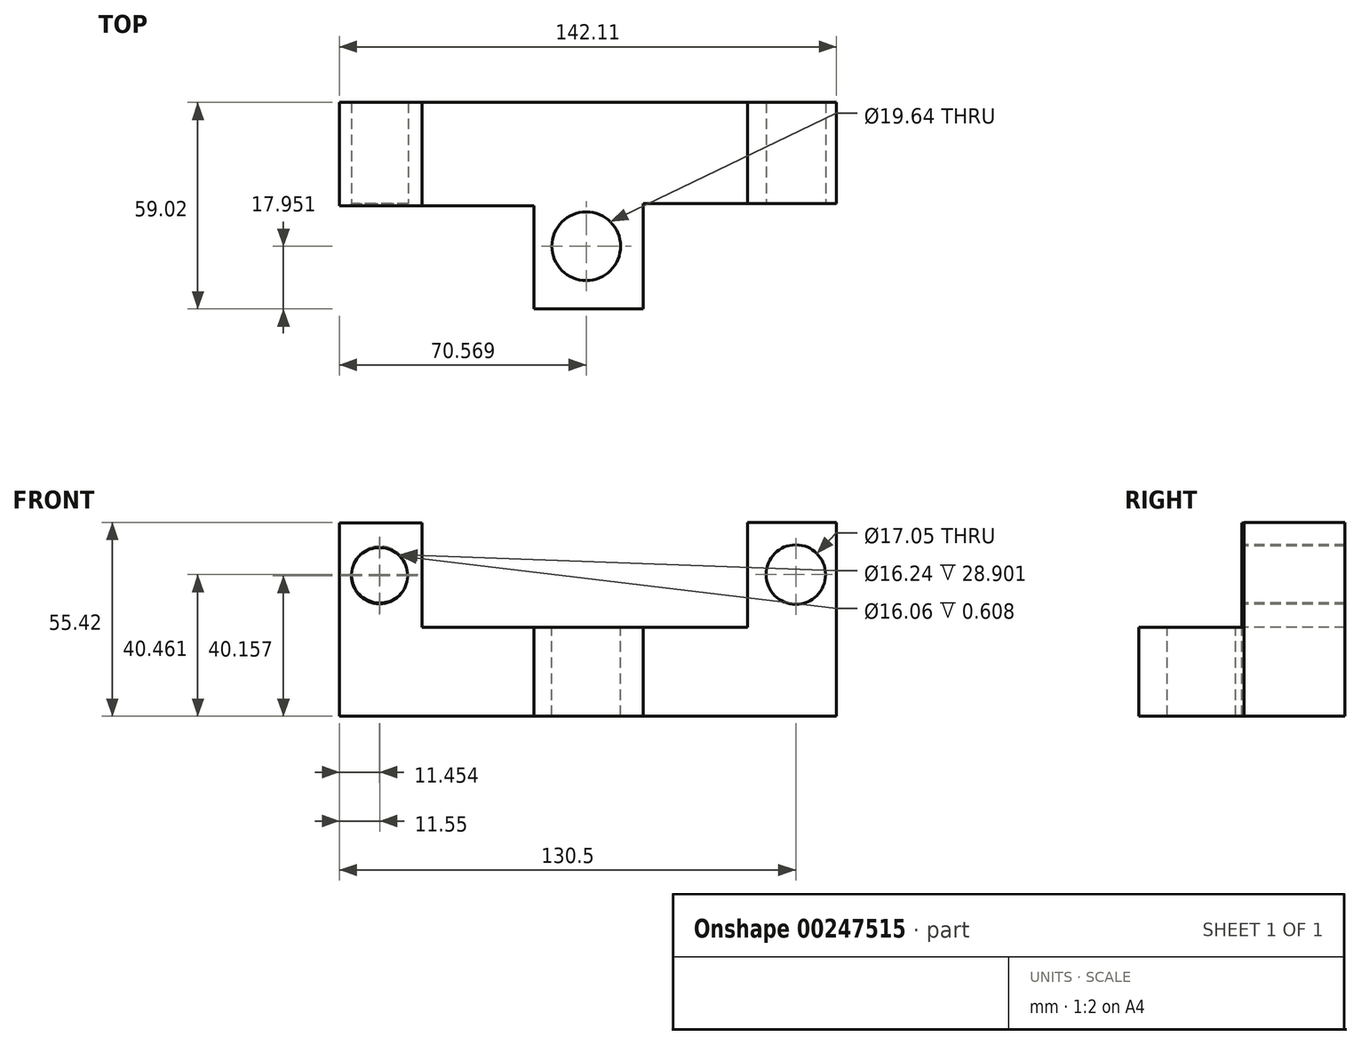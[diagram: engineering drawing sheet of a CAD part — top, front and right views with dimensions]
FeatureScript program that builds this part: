
annotation { "Feature Type Name" : "Feature", "Feature Type Description" : "" }
export const myFeature = defineFeature(function(context is Context, id is Id, definition is map)
    precondition{}
    {
        {
            var Q0;
            Q0=qCreatedBy(makeId("Top.planeOp"),FACE);
            var sketch = newSketch(context, id + "F0", { "sketchPlane" : qUnion([Q0])});
            skLineSegment(sketch, "E0.bottom", {"start": v(-43.05, 28.9) * mm, "end": v(50.04, 28.9) * mm});
            skLineSegment(sketch, "E0.top", {"start": v(-43.05, -30.12) * mm, "end": v(50.04, -30.12) * mm});
            skLineSegment(sketch, "E0.left", {"start": v(-43.05, 28.9) * mm, "end": v(-43.05, -30.12) * mm});
            skLineSegment(sketch, "E0.right", {"start": v(50.04, 28.9) * mm, "end": v(50.04, -30.12) * mm});
            skSolve(sketch);
        }
        {
            var Q0;
            Q0 = qSketchRegion(id + "F0", true);
            extrude(context, id + "F1", {"entities" : qUnion([Q0]), "depth" : 25.4 * mm});
        }
        {
            var Q0;
            Q0=makeQuery(id+"F1.opExtrude","CAP_FACE",FACE,{"disambiguationData":[OSD([sQuery(id+"F0.wireOp",EDGE,"E0.bottom"),sQuery(id+"F0.wireOp",EDGE,"E0.top"),sQuery(id+"F0.wireOp",EDGE,"E0.left"),sQuery(id+"F0.wireOp",EDGE,"E0.right")])],"isStart":false});
            var sketch = newSketch(context, id + "F2", { "sketchPlane" : qUnion([Q0])});
            skLineSegment(sketch, "E1", {"start": v(-43.05, -0.6) * mm, "end": v(-11.1, -0.6) * mm});
            skLineSegment(sketch, "E2", {"start": v(-11.1, -0.6) * mm, "end": v(-11.1, -30.12) * mm});
            skLineSegment(sketch, "E3", {"start": v(20.23, 0) * mm, "end": v(20.23, -30.12) * mm});
            skLineSegment(sketch, "E4", {"start": v(20.23, -30.12) * mm, "end": v(-11.1, -30.12) * mm});
            skLineSegment(sketch, "E5", {"start": v(20.23, 0) * mm, "end": v(50.04, 0) * mm});
            skLineSegment(sketch, "E6", {"start": v(50.04, 0) * mm, "end": v(50.04, -30.12) * mm});
            skLineSegment(sketch, "E7", {"start": v(50.04, -30.12) * mm, "end": v(-43.05, -30.12) * mm});
            skLineSegment(sketch, "E8", {"start": v(-43.05, -30.12) * mm, "end": v(-43.05, -0.6) * mm});
            skSolve(sketch);
        }
        {
            var Q0;
            {var subQ0=sQuery(id+"F2.wireOp",EDGE,"E3");Q0=makeQuery(id+"F2.imprint","IMPRINT",FACE,{"disambiguationData":[TD([[makeQuery(id+"F2.imprint","IMPRINT",EDGE,{"derivedFrom":subQ0}),1.0]])]});}
            var Q1;
            Q1=makeQuery(id+"F2.imprint","IMPRINT",FACE,{"disambiguationData":[TD([[makeQuery(id+"F2.imprint","IMPRINT",EDGE,{"derivedFrom":sQuery(id+"F2.wireOp",EDGE,"E1")}),-1.0]])]});
            extrude(context, id + "F3", {"entities" : qUnion([Q0, Q1]), "operationType" : NewBodyOperationType.REMOVE, "oppositeDirection" : true, "depth" : 25.4 * mm});
        }
        {
            var Q0;
            Q0=makeQuery(id+"F1.opExtrude","SWEPT_FACE",FACE,{"disambiguationData":[OSD([sQuery(id+"F0.wireOp",EDGE,"E0.left")])]});
            var sketch = newSketch(context, id + "F4", { "sketchPlane" : qUnion([Q0])});
            skLineSegment(sketch, "E9", {"start": v(0.6, 0) * mm, "end": v(0.6, 55.22) * mm});
            skLineSegment(sketch, "E10", {"start": v(0.6, 55.22) * mm, "end": v(-28.9, 55.22) * mm});
            skLineSegment(sketch, "E11", {"start": v(-28.9, 55.22) * mm, "end": v(-28.9, 0) * mm});
            skLineSegment(sketch, "E12", {"start": v(-28.9, 0) * mm, "end": v(0, 0) * mm});
            skLineSegment(sketch, "E13", {"start": v(0.6, 0) * mm, "end": v(-28.9, 0) * mm});
            skLineSegment(sketch, "E14", {"start": v(0, 0) * mm, "end": v(0.6, 55.22) * mm});
            skLineSegment(sketch, "E15", {"start": v(-28.9, 55.22) * mm, "end": v(0.6, 55.22) * mm});
            skSolve(sketch);
        }
        {
            var Q0;
            Q0 = qSketchRegion(id + "F4", true);
            extrude(context, id + "F5", {"entities" : qUnion([Q0]), "operationType" : NewBodyOperationType.ADD, "depth" : 23.62 * mm});
        }
        {
            var Q0;
            Q0=makeQuery(id+"F1.opExtrude","SWEPT_FACE",FACE,{"disambiguationData":[OSD([sQuery(id+"F0.wireOp",EDGE,"E0.right")])]});
            var sketch = newSketch(context, id + "F6", { "sketchPlane" : qUnion([Q0])});
            skLineSegment(sketch, "E16", {"start": v(28.9, 0) * mm, "end": v(28.9, 55.42) * mm});
            skLineSegment(sketch, "E17", {"start": v(28.9, 55.42) * mm, "end": v(0, 55.42) * mm});
            skLineSegment(sketch, "E18", {"start": v(0, 55.42) * mm, "end": v(0, 0) * mm});
            skLineSegment(sketch, "E19", {"start": v(0, 0) * mm, "end": v(28.9, 0) * mm});
            skSolve(sketch);
        }
        {
            var Q0;
            Q0 = qSketchRegion(id + "F6", true);
            extrude(context, id + "F7", {"entities" : qUnion([Q0]), "operationType" : NewBodyOperationType.ADD, "depth" : 25.4 * mm});
        }
        {
            var Q0;
            Q0=makeQuery(id+"F1.opExtrude","CAP_FACE",FACE,{"disambiguationData":[OSD([sQuery(id+"F0.wireOp",EDGE,"E0.bottom"),sQuery(id+"F0.wireOp",EDGE,"E0.top"),sQuery(id+"F0.wireOp",EDGE,"E0.left"),sQuery(id+"F0.wireOp",EDGE,"E0.right")])],"isStart":false});
            var sketch = newSketch(context, id + "F8", { "sketchPlane" : qUnion([Q0])});
            skCircle(sketch, "E20", {"center": v(3.9, -12.17) * mm, "radius": 9.82 * mm});
            skSolve(sketch);
        }
        {
            var Q0;
            Q0 = qSketchRegion(id + "F8", true);
            extrude(context, id + "F9", {"entities" : qUnion([Q0]), "operationType" : NewBodyOperationType.REMOVE, "oppositeDirection" : true, "depth" : 33.53 * mm});
        }
        {
            var Q0;
            Q0=qCreatedBy(makeId("Front.planeOp"),FACE);
            var sketch = newSketch(context, id + "F10", { "sketchPlane" : qUnion([Q0])});
            skCircle(sketch, "E21", {"center": v(-55.12, 40.46) * mm, "radius": 8.12 * mm});
            skCircle(sketch, "E22", {"center": v(63.83, 40.46) * mm, "radius": 8.52 * mm});
            skSolve(sketch);
        }
        {
            var Q0;
            Q0 = qSketchRegion(id + "F10", true);
            extrude(context, id + "F11", {"entities" : qUnion([Q0]), "operationType" : NewBodyOperationType.REMOVE, "oppositeDirection" : true, "depth" : 38.1 * mm});
        }
        {
            var Q0;
            Q0=qCreatedBy(makeId("Front.planeOp"),FACE);
            var sketch = newSketch(context, id + "F12", { "sketchPlane" : qUnion([Q0])});
            skCircle(sketch, "E23", {"center": v(-55.22, 40.16) * mm, "radius": 8.03 * mm});
            skSolve(sketch);
        }
        {
            var Q0;
            Q0 = qSketchRegion(id + "F12", true);
            extrude(context, id + "F13", {"entities" : qUnion([Q0]), "operationType" : NewBodyOperationType.REMOVE, "depth" : 60.96 * mm});
        }
    });
